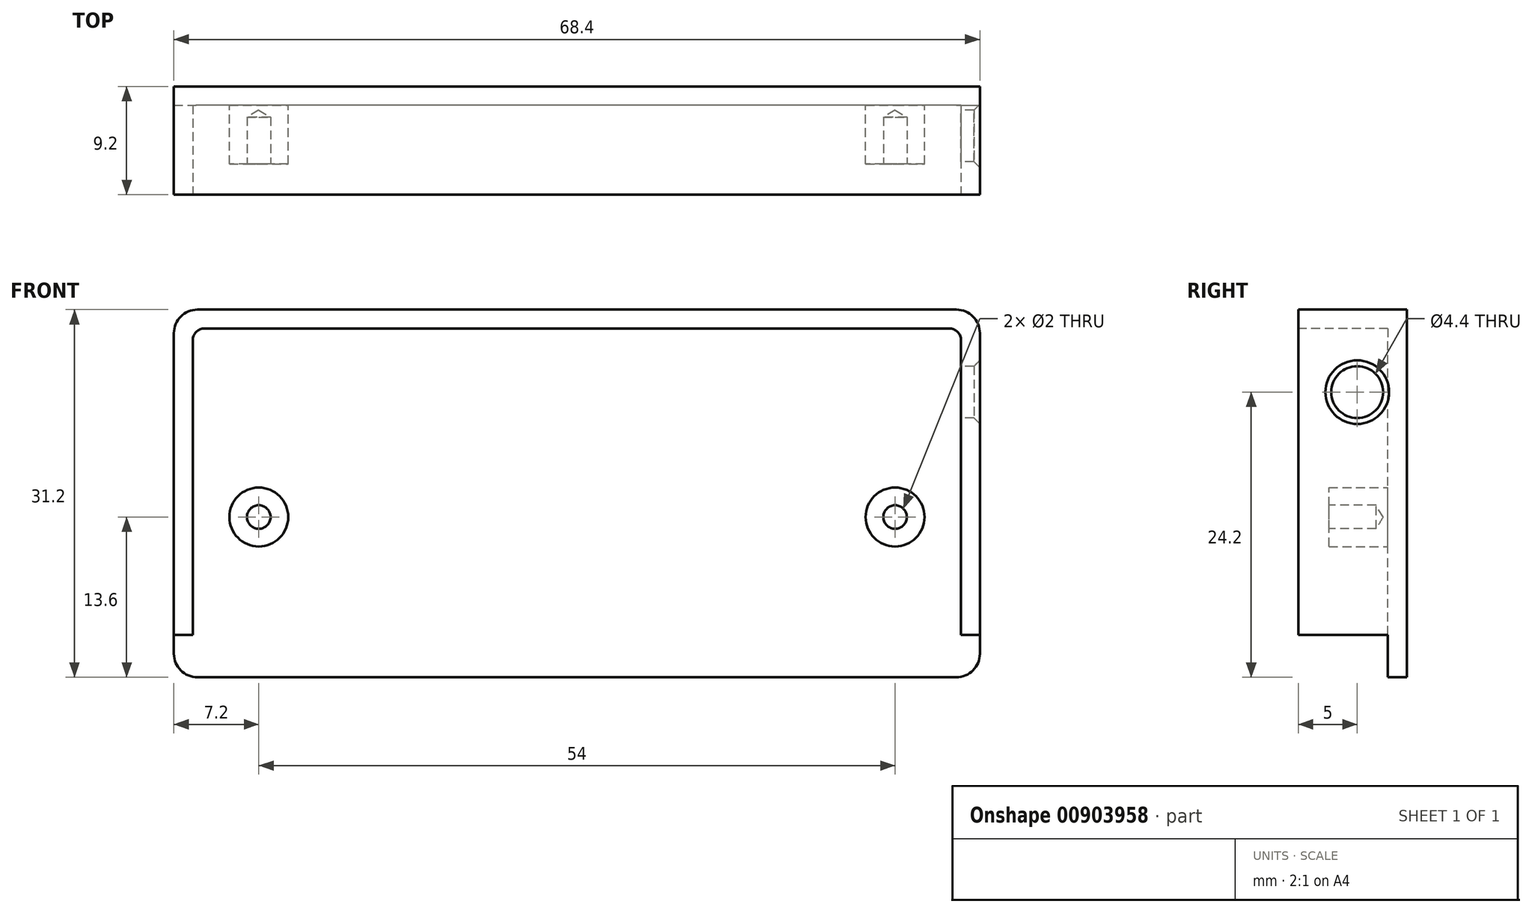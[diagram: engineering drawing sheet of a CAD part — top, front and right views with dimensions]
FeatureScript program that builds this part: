
annotation { "Feature Type Name" : "Feature", "Feature Type Description" : "" }
export const myFeature = defineFeature(function(context is Context, id is Id, definition is map)
    precondition{}
    {
        {
            var Q0;
            Q0=qCreatedBy(makeId("Front.planeOp"),FACE);
            var sketch = newSketch(context, id + "F0", { "sketchPlane" : qUnion([Q0])});
            skLineSegment(sketch, "E0.bottom", {"start": v(34.2, -15.6) * mm, "end": v(-34.2, -15.6) * mm});
            skLineSegment(sketch, "E0.top", {"start": v(34.2, 15.6) * mm, "end": v(-34.2, 15.6) * mm});
            skLineSegment(sketch, "E0.left", {"start": v(34.2, -15.6) * mm, "end": v(34.2, 15.6) * mm});
            skLineSegment(sketch, "E0.right", {"start": v(-34.2, -15.6) * mm, "end": v(-34.2, 15.6) * mm});
            skPoint(sketch, "E0.middle", {"position": v(0, 0) * mm});
            skSolve(sketch);
        }
        {
            var Q0;
            Q0 = qSketchRegion(id + "F0", true);
            extrude(context, id + "F1", {"entities" : qUnion([Q0]), "depth" : 9.2 * mm, "offsetDistance" : 25 * mm});
        }
        {
            var Q0;
            Q0=makeQuery(id+"F1.opExtrude","CAP_FACE",FACE,{"disambiguationData":[OSD([sQuery(id+"F0.wireOp",EDGE,"E0.bottom"),sQuery(id+"F0.wireOp",EDGE,"E0.top"),sQuery(id+"F0.wireOp",EDGE,"E0.left"),sQuery(id+"F0.wireOp",EDGE,"E0.right")])],"isStart":false});
            var sketch = newSketch(context, id + "F2", { "sketchPlane" : qUnion([Q0])});
            skLineSegment(sketch, "E1.top", {"start": v(31.6, 14) * mm, "end": v(-31.6, 14) * mm});
            skLineSegment(sketch, "E1.left", {"start": v(32.6, -12) * mm, "end": v(32.6, 13) * mm});
            skLineSegment(sketch, "E1.right", {"start": v(-32.6, -12) * mm, "end": v(-32.6, 13) * mm});
            skPoint(sketch, "E1.middle", {"position": v(0, 1) * mm});
            skCircle(sketch, "E2", {"center": v(-31.6, 13) * mm, "radius": 1 * mm});
            skPoint(sketch, "E2.first.point", {"position": v(-32.6, 13) * mm});
            skPoint(sketch, "E2.second.point", {"position": v(-31.6, 14) * mm});
            skPoint(sketch, "E2.third.point", {"position": v(-30.68, 12.62) * mm});
            skCircle(sketch, "E3", {"center": v(31.6, 13) * mm, "radius": 1 * mm});
            skPoint(sketch, "E3.first.point", {"position": v(32.6, 13) * mm});
            skPoint(sketch, "E3.second.point", {"position": v(31.6, 14) * mm});
            skPoint(sketch, "E3.third.point", {"position": v(30.96, 12.23) * mm});
            skPoint(sketch, "E4.orphan", {"position": v(-32.6, 14) * mm});
            skPoint(sketch, "E5.orphan", {"position": v(32.6, 14) * mm});
            skLineSegment(sketch, "E6.bottom", {"start": v(-34.2, -12) * mm, "end": v(-32.6, -12) * mm});
            skLineSegment(sketch, "E6.top", {"start": v(-34.2, -15.6) * mm, "end": v(34.2, -15.6) * mm});
            skLineSegment(sketch, "E6.left", {"start": v(-34.2, -12) * mm, "end": v(-34.2, -15.6) * mm});
            skLineSegment(sketch, "E6.right", {"start": v(34.2, -12) * mm, "end": v(34.2, -15.6) * mm});
            skLineSegment(sketch, "E7.trimOffspring", {"start": v(32.6, -12) * mm, "end": v(34.2, -12) * mm});
            skSolve(sketch);
        }
        {
            var Q0;
            Q0 = qSketchRegion(id + "F2", true);
            extrude(context, id + "F3", {"entities" : qUnion([Q0]), "operationType" : NewBodyOperationType.REMOVE, "oppositeDirection" : true, "depth" : 7.6 * mm, "offsetDistance" : 25 * mm});
        }
        {
            var Q0;
            Q0=makeQuery(id+"F1.opExtrude","SWEPT_EDGE",EDGE,{"disambiguationData":[OSD([sQuery(id+"F0.wireOp",EDGE,"E0.top"),sQuery(id+"F0.wireOp",EDGE,"E0.left")])]});
            fillet(context, id + "F4", {"entities" : qUnion([Q0]), "radius" : 2 * mm, "tangentPropagation" : true, "allowEdgeOverflow" : false});
        }
        {
            var Q0;
            Q0=makeQuery(id+"F1.opExtrude","SWEPT_EDGE",EDGE,{"disambiguationData":[OSD([sQuery(id+"F0.wireOp",EDGE,"E0.top"),sQuery(id+"F0.wireOp",EDGE,"E0.right")])]});
            var Q1;
            Q1=makeQuery(id+"F1.opExtrude","SWEPT_EDGE",EDGE,{"disambiguationData":[OSD([sQuery(id+"F0.wireOp",EDGE,"E0.bottom"),sQuery(id+"F0.wireOp",EDGE,"E0.right")])]});
            fillet(context, id + "F5", {"entities" : qUnion([Q0, Q1]), "radius" : 2 * mm, "tangentPropagation" : true, "allowEdgeOverflow" : false});
        }
        {
            var Q0;
            Q0=makeQuery(id+"F1.opExtrude","SWEPT_EDGE",EDGE,{"disambiguationData":[OSD([sQuery(id+"F0.wireOp",EDGE,"E0.bottom"),sQuery(id+"F0.wireOp",EDGE,"E0.left")])]});
            fillet(context, id + "F6", {"entities" : qUnion([Q0]), "radius" : 2 * mm, "tangentPropagation" : true, "allowEdgeOverflow" : false});
        }
        {
            var Q0;
            Q0=makeQuery(id+"F3.boolean.opBoolean","COPY",FACE,{"derivedFrom":makeQuery(id+"F3.opExtrude","CAP_FACE",FACE,{"disambiguationData":[OSD([sQuery(id+"F2.wireOp",EDGE,"E1.top"),sQuery(id+"F2.wireOp",EDGE,"E1.left"),sQuery(id+"F2.wireOp",EDGE,"E1.right"),sQuery(id+"F2.wireOp",EDGE,"E2"),sQuery(id+"F2.wireOp",EDGE,"E3"),sQuery(id+"F2.wireOp",EDGE,"E6.bottom"),sQuery(id+"F2.wireOp",EDGE,"E6.top"),sQuery(id+"F2.wireOp",EDGE,"E6.left"),sQuery(id+"F2.wireOp",EDGE,"E6.right"),sQuery(id+"F2.wireOp",EDGE,"E7.trimOffspring")])],"isStart":false})});
            var sketch = newSketch(context, id + "F7", { "sketchPlane" : qUnion([Q0])});
            skCircle(sketch, "E8", {"center": v(-27, -2) * mm, "radius": 2.5 * mm});
            skPoint(sketch, "E8.first.point", {"position": v(-29.27, -3.04) * mm});
            skPoint(sketch, "E8.second.point", {"position": v(-26.63, -4.47) * mm});
            skPoint(sketch, "E8.third.point", {"position": v(-27.02, 0.5) * mm});
            skCircle(sketch, "E9", {"center": v(27, -2) * mm, "radius": 2.5 * mm});
            skPoint(sketch, "E9.first.point", {"position": v(26.98, 0.5) * mm});
            skPoint(sketch, "E9.second.point", {"position": v(29.46, -1.55) * mm});
            skPoint(sketch, "E9.third.point", {"position": v(27.02, 0.5) * mm});
            skSolve(sketch);
        }
        {
            var Q0;
            Q0 = qSketchRegion(id + "F7", true);
            extrude(context, id + "F8", {"entities" : qUnion([Q0]), "operationType" : NewBodyOperationType.ADD, "depth" : 5 * mm, "offsetDistance" : 25 * mm});
        }
        {
            var Q0;
            Q0=makeQuery(id+"F8.opExtrude","CAP_FACE",FACE,{"disambiguationData":[OSD([sQuery(id+"F7.wireOp",EDGE,"E8")])],"isStart":false});
            var sketch = newSketch(context, id + "F9", { "sketchPlane" : qUnion([Q0])});
            skPoint(sketch, "E10", {"position": v(-27, -2) * mm});
            skSolve(sketch);
        }
        {
            var Q0;
            Q0=sQuery(id+"F9.wireOp",VERTEX,"E10");
            var Q1;
            Q1=makeQuery(id+"F1.opExtrude","SWEPT_BODY",BODY,{"disambiguationData":[OSD([sQuery(id+"F0.wireOp",EDGE,"E0.bottom"),sQuery(id+"F0.wireOp",EDGE,"E0.top"),sQuery(id+"F0.wireOp",EDGE,"E0.left"),sQuery(id+"F0.wireOp",EDGE,"E0.right")])]});
            hole(context, id + "F10", {"style" : HoleStyle.SIMPLE, "endStyle" : HoleEndStyle.BLIND, "holeDiameter" : 2 * mm, "majorDiameter" : 5 * mm, "holeDepth" : 4 * mm, "isTappedThrough" : true, "tappedDepth" : 12 * mm, "tapClearance" : 3, "locations" : qUnion([Q0]), "scope" : qUnion([Q1])});
        }
        {
            var Q0;
            Q0=makeQuery(id+"F8.opExtrude","CAP_FACE",FACE,{"disambiguationData":[OSD([sQuery(id+"F7.wireOp",EDGE,"E9")])],"isStart":false});
            var sketch = newSketch(context, id + "F11", { "sketchPlane" : qUnion([Q0])});
            skPoint(sketch, "E11", {"position": v(27, -2) * mm});
            skSolve(sketch);
        }
        {
            var Q0;
            Q0=sQuery(id+"F11.wireOp",VERTEX,"E11");
            var Q1;
            Q1=makeQuery(id+"F1.opExtrude","SWEPT_BODY",BODY,{"disambiguationData":[OSD([sQuery(id+"F0.wireOp",EDGE,"E0.bottom"),sQuery(id+"F0.wireOp",EDGE,"E0.top"),sQuery(id+"F0.wireOp",EDGE,"E0.left"),sQuery(id+"F0.wireOp",EDGE,"E0.right")])]});
            hole(context, id + "F12", {"style" : HoleStyle.SIMPLE, "endStyle" : HoleEndStyle.BLIND, "holeDiameter" : 2 * mm, "majorDiameter" : 5 * mm, "holeDepth" : 4 * mm, "isTappedThrough" : true, "tappedDepth" : 12 * mm, "tapClearance" : 3, "locations" : qUnion([Q0]), "scope" : qUnion([Q1])});
        }
        {
            var Q0;
            Q0=makeQuery(id+"F3.boolean.opBoolean","COPY",FACE,{"derivedFrom":makeQuery(id+"F3.opExtrude","SWEPT_FACE",FACE,{"disambiguationData":[OSD([sQuery(id+"F2.wireOp",EDGE,"E1.left")])]})});
            var sketch = newSketch(context, id + "F13", { "sketchPlane" : qUnion([Q0])});
            skCircle(sketch, "E12", {"center": v(4.2, 8.6) * mm, "radius": 2.2 * mm});
            skSolve(sketch);
        }
        {
            var Q0;
            Q0 = qSketchRegion(id + "F13", true);
            extrude(context, id + "F14", {"entities" : qUnion([Q0]), "operationType" : NewBodyOperationType.REMOVE, "endBound" : BoundingType.THROUGH_ALL, "oppositeDirection" : true, "depth" : 25 * mm, "offsetDistance" : 25 * mm});
        }
        {
            var Q0;
            Q0=makeQuery(id+"F14.boolean.opBoolean","INTERSECT",EDGE,{"derivedFrom":[makeQuery(id+"F1.opExtrude","SWEPT_FACE",FACE,{"disambiguationData":[OSD([sQuery(id+"F0.wireOp",EDGE,"E0.left")])]}),makeQuery(id+"F14.opExtrude","SWEPT_FACE",FACE,{"disambiguationData":[OSD([sQuery(id+"F13.wireOp",EDGE,"E12")])]})]});
            chamfer(context, id + "F15", {"entities" : qUnion([Q0]), "width" : 0.5 * mm, "tangentPropagation" : true});
        }
    });
